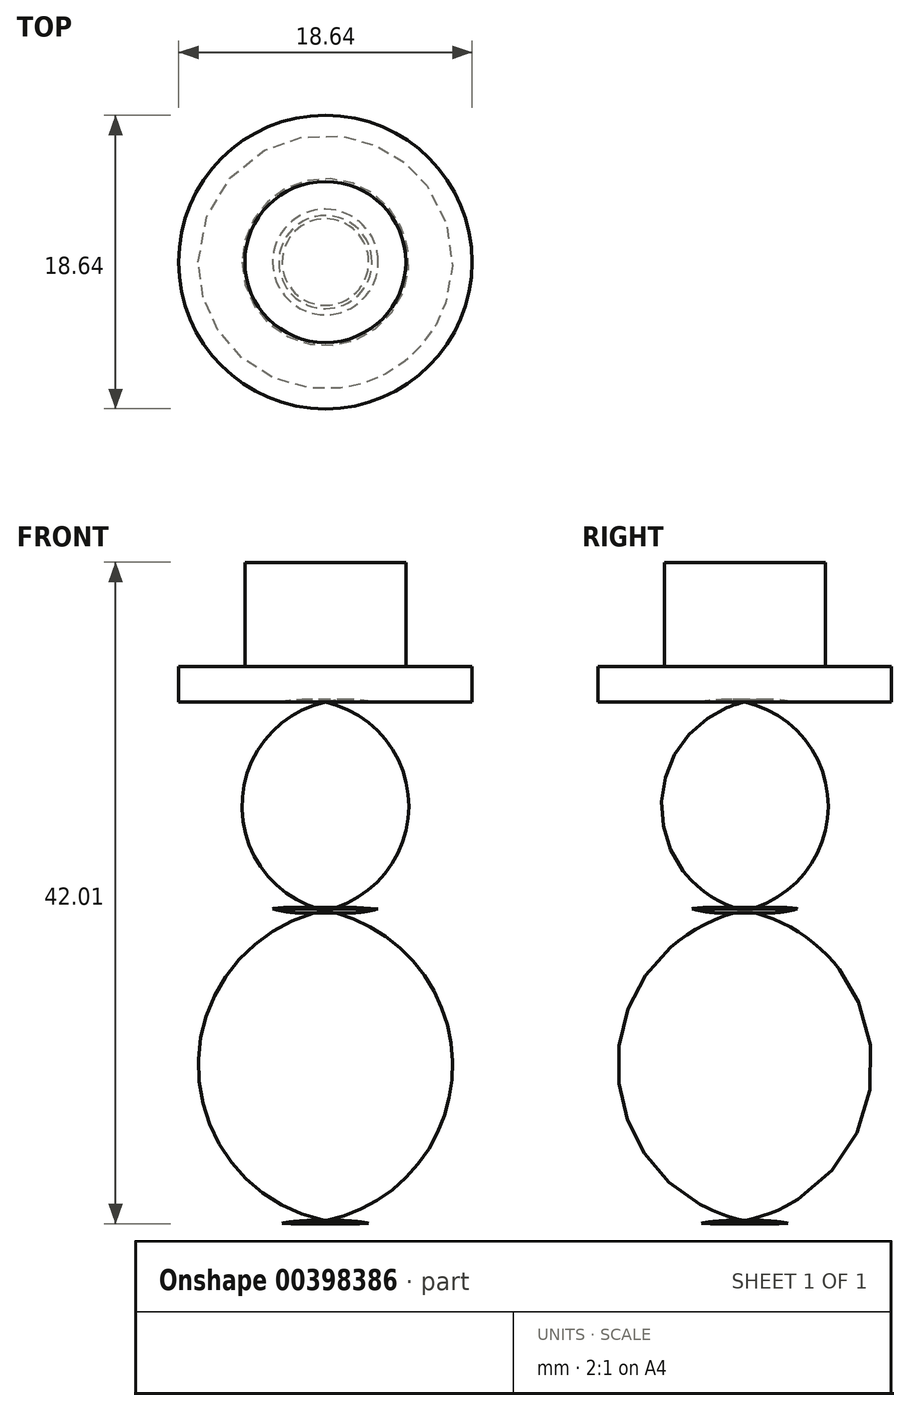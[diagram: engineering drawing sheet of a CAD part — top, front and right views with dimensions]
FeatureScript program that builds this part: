
annotation { "Feature Type Name" : "Feature", "Feature Type Description" : "" }
export const myFeature = defineFeature(function(context is Context, id is Id, definition is map)
    precondition{}
    {
        {
            var Q0;
            Q0=qCreatedBy(makeId("Right.planeOp"),FACE);
            var sketch = newSketch(context, id + "F0", { "sketchPlane" : qUnion([Q0])});
            skArc(sketch, "E0", {"start": v(0, -72.52) * mm, "mid": v(21.84, -51.59) * mm, "end": v(0, -30.65) * mm});
            skArc(sketch, "E1", {"start": v(0, -30.65) * mm, "mid": v(18.7, -15.32) * mm, "end": v(0, 0) * mm});
            skArc(sketch, "E2", {"start": v(0, 0) * mm, "mid": v(12.85, 10.3) * mm, "end": v(0, 20.59) * mm});
            skLineSegment(sketch, "E3", {"start": v(0, 20.59) * mm, "end": v(0, -72.52) * mm});
            skLineSegment(sketch, "E4", {"start": v(0, 20.59) * mm, "end": v(14.5, 20.59) * mm});
            skLineSegment(sketch, "E5", {"start": v(14.5, 20.59) * mm, "end": v(14.5, 24.1) * mm});
            skLineSegment(sketch, "E6", {"start": v(14.5, 24.1) * mm, "end": v(7.95, 24.1) * mm});
            skLineSegment(sketch, "E7", {"start": v(7.95, 24.1) * mm, "end": v(7.95, 34.4) * mm});
            skLineSegment(sketch, "E8", {"start": v(7.95, 34.4) * mm, "end": v(0, 34.4) * mm});
            skLineSegment(sketch, "E9", {"start": v(0, 34.4) * mm, "end": v(0, 20.59) * mm});
            skSolve(sketch);
        }
        {
            var Q0;
            Q0 = qSketchRegion(id + "F0", true);
            var Q1;
            Q1=sQuery(id+"F0.wireOp",EDGE,"E3");
            revolve(context, id + "F1", {"entities" : qUnion([Q0]), "axis" : qUnion([Q1]), "revolveType" : RevolveType.FULL});
        }
        {
            var Q0;
            Q0=qCreatedBy(makeId("Right.planeOp"),FACE);
            var sketch = newSketch(context, id + "F2", { "sketchPlane" : qUnion([Q0])});
            skCircle(sketch, "E10", {"center": v(5.61, 14.04) * mm, "radius": 2.16 * mm});
            skCircle(sketch, "E11.MirrorC", {"center": v(-5.61, 14.04) * mm, "radius": 2.16 * mm});
            skCircle(sketch, "E12", {"center": v(8.66, 7.72) * mm, "radius": 1.36 * mm});
            skCircle(sketch, "E13", {"center": v(3.04, 3.98) * mm, "radius": 1.42 * mm});
            skCircle(sketch, "E14.MirrorC", {"center": v(-3.04, 3.98) * mm, "radius": 1.42 * mm});
            skCircle(sketch, "E15.MirrorC", {"center": v(-8.66, 7.72) * mm, "radius": 1.36 * mm});
            skCircle(sketch, "E16", {"center": v(0, -10.3) * mm, "radius": 3.98 * mm});
            skCircle(sketch, "E17", {"center": v(0, -23.16) * mm, "radius": 4.17 * mm});
            skSolve(sketch);
        }
        {
            var Q0;
            Q0=sQuery(id+"F2.wireOp",VERTEX,"E10.center");
            var Q1;
            Q1=sQuery(id+"F2.wireOp",VERTEX,"E11.MirrorC.center");
            var Q2;
            Q2=sQuery(id+"F2.wireOp",VERTEX,"22ffb976-12cd-48cb-b9d4-7d6511a891970.MirrorC.center");
            var Q3;
            Q3=sQuery(id+"F2.wireOp",VERTEX,"40a27d30-eace-4931-b77a-060d25d1ac810.MirrorC.center");
            var Q4;
            Q4=sQuery(id+"F2.wireOp",VERTEX,"2qdXHBvo-mbEa-EilG-k1nW-V8PzviKZs1mG.center");
            var Q5;
            Q5=sQuery(id+"F2.wireOp",VERTEX,"cbEjbfUY-BjZQ-19Ft-xJ4N-ivtHlbx6fcxS.center");
            var Q6;
            Q6=sQuery(id+"F2.wireOp",VERTEX,"rjV9WY2F-0RxX-Pi7i-5AUj-KuL7FDstXtyV.center");
            var Q7;
            Q7=sQuery(id+"F2.wireOp",VERTEX,"W6mIunFS-P0bN-66Ac-0A36-H3ngWt38UN2R.center");
            var Q8;
            Q8=sQuery(id+"F2.wireOp",VERTEX,"E14.MirrorC.center");
            var Q9;
            Q9=sQuery(id+"F2.wireOp",VERTEX,"E15.MirrorC.center");
            var Q10;
            Q10=sQuery(id+"F2.wireOp",VERTEX,"E13.center");
            var Q11;
            Q11=sQuery(id+"F2.wireOp",VERTEX,"E12.center");
            var Q12;
            Q12=sQuery(id+"F2.wireOp",VERTEX,"E16.center");
            var Q13;
            Q13=sQuery(id+"F2.wireOp",VERTEX,"E17.center");
            var Q14;
            Q14=makeQuery(id+"F1.opRevolve","SWEPT_BODY",BODY,{"disambiguationData":[OSD([sQuery(id+"F0.wireOp",EDGE,"E0"),sQuery(id+"F0.wireOp",EDGE,"E1"),sQuery(id+"F0.wireOp",EDGE,"E2"),sQuery(id+"F0.wireOp",EDGE,"E3"),sQuery(id+"F0.wireOp",EDGE,"nq5EaUev-2r0F-lyYc-Dw9M-JZO1rCt7FYxo"),sQuery(id+"F0.wireOp",EDGE,"BHdWa128-JCRL-EqQ1-wUAB-zWHKtik91RzL")])]});
            hole(context, id + "F3", {"style" : HoleStyle.SIMPLE, "endStyle" : HoleEndStyle.THROUGH, "holeDiameter" : 6.35 * mm, "isTappedThrough" : true, "tappedDepth" : 12.7 * mm, "tapClearance" : 3, "locations" : qUnion([Q0, Q1, Q2, Q3, Q4, Q5, Q6, Q7, Q8, Q9, Q10, Q11, Q12, Q13]), "scope" : qUnion([Q14])});
        }
        {
            var Q0;
            Q0=makeQuery(id+"F1.opRevolve","SWEPT_BODY",BODY,{"disambiguationData":[OSD([sQuery(id+"F0.wireOp",EDGE,"E0"),sQuery(id+"F0.wireOp",EDGE,"E1"),sQuery(id+"F0.wireOp",EDGE,"E2"),sQuery(id+"F0.wireOp",EDGE,"E3"),sQuery(id+"F0.wireOp",EDGE,"E4"),sQuery(id+"F0.wireOp",EDGE,"E5"),sQuery(id+"F0.wireOp",EDGE,"E6"),sQuery(id+"F0.wireOp",EDGE,"E7"),sQuery(id+"F0.wireOp",EDGE,"E8"),sQuery(id+"F0.wireOp",EDGE,"E9")])]});
            var Q1;
            Q1=makeQuery(id+"F1.opRevolve","SWEPT_VERTEX",VERTEX,{"disambiguationData":[OSD([sQuery(id+"F0.wireOp",EDGE,"E0"),sQuery(id+"F0.wireOp",EDGE,"E3")])]});
            transform(context, id + "F4", {"entities" : qUnion([Q0]), "transformType" : TransformType.SCALE_UNIFORMLY, "scale" : 2.25 / 3.5, "scalePoint" : qUnion([Q1]), "makeCopy" : false});
        }
    });
